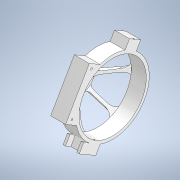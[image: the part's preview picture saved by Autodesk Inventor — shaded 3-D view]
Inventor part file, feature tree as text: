
AUTODESK INVENTOR PART (.ipt)
format: ipt  version: 2020.3 (Build 243373000, 373)  size: 463,360 bytes
history: native  units: mm
features: extrude x15, sketch x15, other x9, plane x6, projected_geometry x3, reference x3, pattern_circular x2, fillet x2
ambient origin geometry x8: Origin, YZ Plane, XZ Plane, XY Plane, X Axis, Y Axis, Z Axis, Center Point
bodies: Solid1 (feature_tree)
feature tree (55):
  other  "Prindere"
  other  "Blocks"
  extrude  "Extrusion1"  Depth=4.0mm
  plane  "Work Plane1"
  sketch  "Sketch3"  dims[d2=4.0mm d3=4.0mm]
  plane  "Work Plane2"
  extrude  "Extrusion2"  Depth=4.0mm
  pattern_circular  "Circular Pattern1"  Count=3  [1 undecoded]
  extrude  "Extrusion3"  Depth=67.5mm TaperAngle=0.0deg
  extrude  "Extrusion4"  Depth=30.0mm
  fillet  "Fillet1"  [1 undecoded]
  fillet  "Fillet2"  Radius=6.0mm
  extrude  "Extrusion6"  Depth=10.0mm
  plane  "Work Plane3"
  extrude  "Extrusion7"  Depth=10.0mm
  pattern_circular  "Circular Pattern2"  Count=3  [1 undecoded]
  extrude  "Extrusion8"  Depth=8.0mm
  extrude  "Extrusion9"  Depth=4.0mm
  extrude  "Extrusion10"  Depth=4.0mm
  sketch  "Sketch13"  dims[d25=10.0mm d26=0.0mm]
  plane  "Work Plane6"
  extrude  "Extrusion11"  Depth=8.0mm
  sketch  "Sketch14"  dims[d27=15.0deg]
  plane  "Work Plane7"
  extrude  "Extrusion12"  Depth=8.0mm
  sketch  "Sketch15"  dims[d28=6.5mm]
  plane  "Work Plane8"
  extrude  "Extrusion13"  Depth=8.0mm
  extrude  "Extrusion14"  Depth=40.0mm TaperAngle=0.0deg
  extrude  "Extrusion15"  Depth=10.0mm
  extrude  "Extrusion16"  Depth=2.5mm
  sketch  "Sketch1"  dims[d0=45.0mm d1=4.0mm]
  other  "Work Axis1"
  other  "Work Axis2"
  sketch  "Sketch5"  dims[d4=4.0mm]
  sketch  "Sketch6"  dims[d5=12.0mm]
  sketch  "Sketch8"  dims[d6=10.0mm d7=0.0mm d8=30.0mm]
  other  "Work Axis3"
  sketch  "Sketch9"  dims[d9=67.5mm d10=6.0mm d11=0.0mm]
  sketch  "Sketch10"  dims[d12=60.0mm d13=360.0deg d15=30.0mm d16=0.0mm d17=6.0mm]
  sketch  "Sketch11"  dims[d18=60.0mm d19=0.0mm d20=10.0mm]
  sketch  "Sketch12"  dims[d21=10.0mm d24=90.0mm]
  projected_geometry  "Projected Loop2"
  sketch  "Sketch16"  dims[d29=1.5mm d30=30.0mm d31=0.0mm]
  reference  "Reference2"
  reference  "Reference3"
  sketch  "Sketch17"  dims[d33=20.0mm d34=360.0deg d36=8.0mm]
  projected_geometry  "Projected Loop3"
  projected_geometry  "Projected Loop4"
  sketch  "Sketch18"  dims[d37=10.0mm d38=0.0mm d39=4.0mm d40=4.0mm d41=8.0mm d42=8.0mm d43=8.0mm d44=40.0mm d45=0.0mm d47=10.0mm d48=2.5mm d49=3.0mm d50=0.0mm d51=0.0mm d52=11.75mm d53=0.0mm d54=4.0mm d55=10.0mm d56=0.0mm d57=10.0mm d58=0.0mm d59=2.5mm d60=2.5mm d61=10.0mm d62=0.0mm d63=4.25mm d64=0.0mm d65=5.0mm d66=8.0mm d67=37.6mm d68=0.0mm]
  reference  "Reference4"
  other  "Prindere:1"
  other  "<userpath>\Documents\Inventor\TheArch\R&D\Beta0\Structura\Prototip\Prototip1.iam"
  other  "Prototip1.iam"
  other  "SG90:1"
note: 3 required parameter values undecoded (feature->parameter linkage not recoverable at this tier; creation-order binding heuristic only, values carry confidence <= 0.55)
